# Revit family: Camera-Security-Panasonic-Super_Dynamic-Weatherproof-H265_Varifocal-Network-Fixed_Box-U1532LSeriesX
name_source: partatom
category: Security Devices
revit_build: Autodesk Revit 2016 (Build: 20190507_1515(x64)
units: mm (PartAtom-declared; Revit-internal decimal feet)

## family parameters
Cut with Voids When Loaded = No
Host = Face
Maintain Annotation Orientation = No
OmniClass Number = 23.85.10.14.11
OmniClass Title = Cameras
Part Type = Normal
Room Calculation Point = No
Round Connector Dimension = Use Diameter
Shared = No

## types (2) — shared parameters
Audio In = No
Audio Out = No
Communication Ports = 10Base-T / 100Base-TX, RJ45 connector
Date Last Modified = 2020/01/07
Day Or Night = Yes
Equipment Abbreviation = SC
Family Version = 1.0.0
HFOV Min 169 = 44.00°
Has POE = Yes
IP Or Analog = IP
Indoor Or Outdoor = Outdoor
Manufacturer = Panasonic
Model Disclaimer = Contact Panasonic for more information
Mounting Positions = Mount Dependent or Surface Mount
No Accessories = Yes
Operational Humidity = 10 to 100 % (no condensation)
Operational Temperature = -30 °C to +50 °C (-22 °F to +122 °F)
Product Documentation Link = https://bizpartner.panasonic.net
Product Material = Paint - Panasonic - i-PRO White
Product Page URL = https://security.panasonic.com
Provide Feedback = https://www.surveymonkey.com
Regulatory Compliance = UL (UL60950-1), c-UL (CSA C22.2 No.60950-1), CE, IEC60950-1, FCC (Part15 ClassA), ICES003 ClassA, EN55032 ClassB, EN55024
Shock Resistance = IK10 (IEC 62262)
Storage Temperature = -30 °C to +50 °C (-22 °F to +122 °F)
Super Dynamic Range = Yes
URL = http://security.panasonic.com
Vandal Resistant = Yes
Voltage DC = 48 V
Water and Dust Resistance = IP66 (IEC 60529), Type 4X (UL50E), NEMA 4X compliant
Width = 114 mm  [stored 0.374016 ft]
Yaw Max = 100.00°
Yaw Min = -190.00°
z Adaptor Box Offset = 0.5 mm  [stored 0.00164042 ft]
z Base Square = Yes
z Camera Center Offset = 7.3 mm
z Camera Center Offset Base = 30 mm  [stored 0.0984252 ft]
z Const CameraYawAxis = 400 mm  [stored 1.31234 ft]
z Const Pan Handle Length = 700 mm  [stored 2.29659 ft]
z Const Tilt Base Length = 250 mm  [stored 0.82021 ft]
z Const Tilt Base2 Length = 500 mm  [stored 1.64042 ft]
z Const Tilt Handle Length = 360 mm  [stored 1.1811 ft]
z Const Yaw Axis Length = 200 mm  [stored 0.656168 ft]
z Const Yaw Base Length = 260 mm  [stored 0.853018 ft]
z Const Yaw Base2 Length = 440 mm  [stored 1.44357 ft]
z Const Yaw Handle Length = 235 mm  [stored 0.770997 ft]
z VV Viewpoint Depth Max = 159.8 mm  [stored 0.524278 ft]
z VV Viewpoint Depth Min = 159.8 mm  [stored 0.524278 ft]
zero-valued in all types: Default Elevation

## per-type parameters (varying)
| type | Angle Of View | Camera Type | Description | HFOV Max 169 | HFOV Max 43 | HFOV Min 43 | Minimum Illumination | Part Description | Power Active | VFOV Max 169 | VFOV Max 43 | VFOV Min 169 | VFOV Min 43 |
| WV-U1532L | 102 | 1 | Security Camera, Super Dynamic, FullHD, VariFocal, Weatherproof, Network, WV-U1532L | 102.00° | 84.00° | 36.00° | 0.100 lx | Security Camera, Super Dynamic, FullHD, VariFocal, Weatherproof, Network, WV-U1532L | 6.7 W | 56.00° | 63.00° | 24.00° | 27.00° |
| WV-U1542L | 103 | 2 | Security Camera, Super Dynamic, 4Mega Pixel, VariFocal, Weatherproof, Network, WV-U1542L | 103.00° | 103.00° | 44.00° | 0.300 lx | Security Camera, Super Dynamic, 4Mega Pixel, VariFocal, Weatherproof, Network, WV-U1542L | 7.2 W | 57.00° | 57.00° | 25.00° | 25.00° |

note: column(s) folded — value = type name in every type: Model, Part Number

note: [stored X ft] marks values corroborated as IEEE doubles in the binary element streams (Revit-internal decimal feet)

## geometry (parser evidence)
native form markers: Blend x2, Sweep x10
no freeform markers — native parametric forms only
